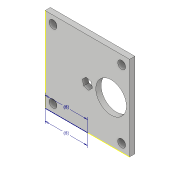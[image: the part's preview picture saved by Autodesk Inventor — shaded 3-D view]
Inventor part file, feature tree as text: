
AUTODESK INVENTOR PART (.ipt)
format: ipt  version: 2019 (Build 230136000, 136)  size: 136,704 bytes
history: native  units: in
note: dims shown in document units (in); Inventor stores cm internally (conversion verified against a paired STEP export)
features: sketch x5, extrude x4
ambient origin geometry x8: Origin, YZ Plane, XZ Plane, XY Plane, X Axis, Y Axis, Z Axis, Center Point
bodies: Solid1 (feature_tree)
feature tree (9):
  extrude  "Extrusion1"  Depth=6.2992in
  extrude  "Extrusion2"  Depth=0.3937in
  sketch  "Sketch3"  dims[d5=0.5906in d6=0.5906in]
  sketch  "Sketch4"  dims[d7=0.5906in d8=0.5906in]
  sketch  "Sketch5"  dims[d9=0.6496in d10=0.5906in d11=0.5906in d12=0.5906in d13=0.5906in d14=0.5906in d15=0.5906in d16=0.3937in d17=0.0in d18=3.1496in d19=3.1496in d20=3.1496in d21=3.1496in d22=3.1496in d23=0.3937in d24=3.1496in d25=1.378in d26=2.2835in d27=0.3937in d28=0.0in d29=0.3937in d30=0.0in]
  extrude  "Extrusion3"  Depth=0.5906in
  extrude  "Extrusion4"  Depth=0.5906in
  sketch  "Sketch1"  dims[d0=6.2992in d1=6.2992in]
  sketch  "Sketch2"  dims[d2=0.3937in d3=0.0in d4=0.5906in]
